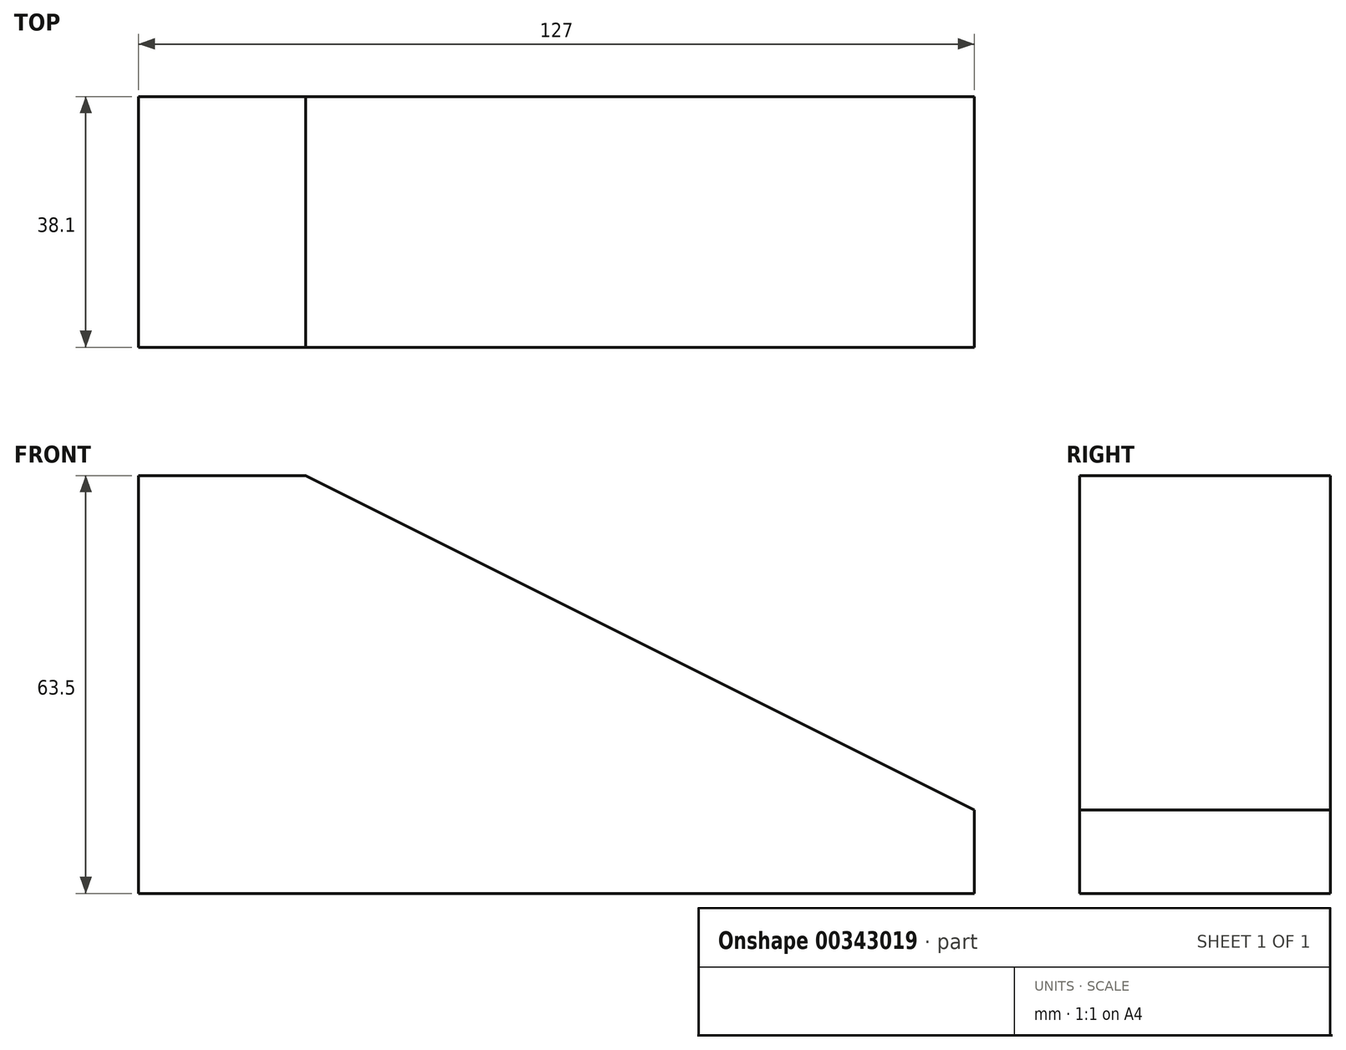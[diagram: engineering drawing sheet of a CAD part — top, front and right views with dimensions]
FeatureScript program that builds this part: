
annotation { "Feature Type Name" : "Feature", "Feature Type Description" : "" }
export const myFeature = defineFeature(function(context is Context, id is Id, definition is map)
    precondition{}
    {
        {
            var Q0;
            Q0=qCreatedBy(makeId("Front.planeOp"),FACE);
            var sketch = newSketch(context, id + "F0", { "sketchPlane" : qUnion([Q0])});
            skLineSegment(sketch, "E0", {"start": v(-66.75, -50.28) * mm, "end": v(60.25, -50.28) * mm});
            skLineSegment(sketch, "E1", {"start": v(-66.75, -50.28) * mm, "end": v(-66.75, 13.22) * mm});
            skLineSegment(sketch, "E2", {"start": v(-66.75, 13.22) * mm, "end": v(-41.35, 13.22) * mm});
            skLineSegment(sketch, "E3", {"start": v(60.25, -50.28) * mm, "end": v(60.25, -37.58) * mm});
            skLineSegment(sketch, "E4", {"start": v(-41.35, 13.22) * mm, "end": v(60.25, -37.58) * mm});
            skSolve(sketch);
        }
        {
            var Q0;
            Q0 = qSketchRegion(id + "F0", true);
            extrude(context, id + "F1", {"entities" : qUnion([Q0]), "depth" : 38.1 * mm});
        }
    });
